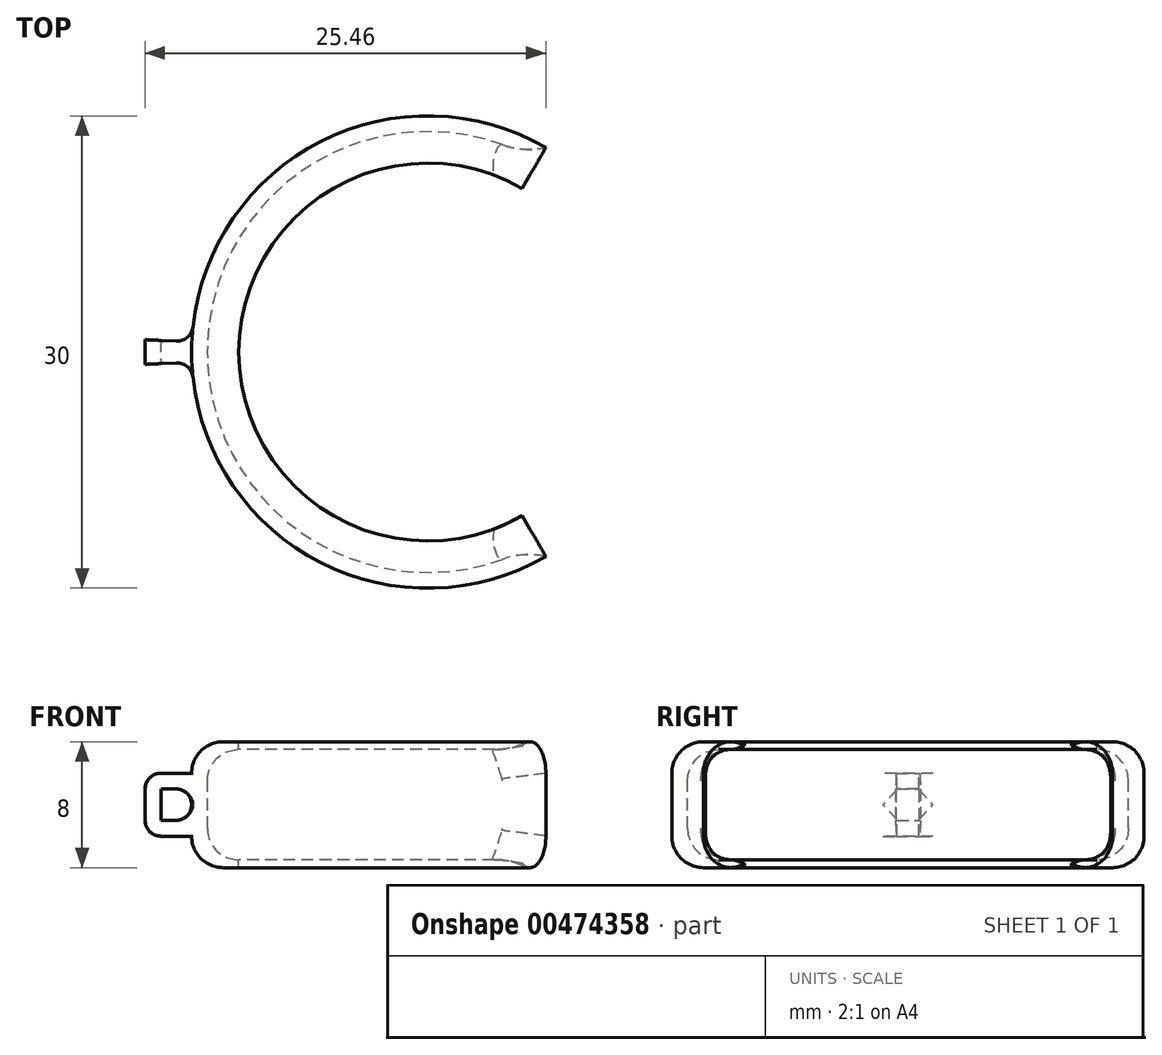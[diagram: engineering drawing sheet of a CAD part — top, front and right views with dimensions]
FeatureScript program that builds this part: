
annotation { "Feature Type Name" : "Feature", "Feature Type Description" : "" }
export const myFeature = defineFeature(function(context is Context, id is Id, definition is map)
    precondition{}
    {
        {
            var Q0;
            Q0=qCreatedBy(makeId("Front.planeOp"),FACE);
            var sketch = newSketch(context, id + "F0", { "sketchPlane" : qUnion([Q0])});
            skLineSegment(sketch, "E0", {"start": v(0, 12.3) * mm, "end": v(0, 0) * mm, "construction": true});
            skLineSegment(sketch, "E1", {"start": v(-12, -3.5) * mm, "end": v(-12, -3.5) * mm});
            skLineSegment(sketch, "E2", {"start": v(-14, 1.5) * mm, "end": v(-14, -1.5) * mm});
            skPoint(sketch, "E3.newPointB", {"position": v(-14, 3.5) * mm});
            skArc(sketch, "E3.filletArc", {"start": v(-12, 3.5) * mm, "mid": v(-13.41, 2.91) * mm, "end": v(-14, 1.5) * mm});
            skPoint(sketch, "E4.newPointA", {"position": v(-14, -3.5) * mm});
            skArc(sketch, "E4.filletArc", {"start": v(-14, -1.5) * mm, "mid": v(-13.41, -2.91) * mm, "end": v(-12, -3.5) * mm});
            skLineSegment(sketch, "E5", {"start": v(-12, 4) * mm, "end": v(-13, 4) * mm});
            skLineSegment(sketch, "E6", {"start": v(-15, 2) * mm, "end": v(-15, -2) * mm});
            skLineSegment(sketch, "E7", {"start": v(-13, -4) * mm, "end": v(-12, -4) * mm});
            skLineSegment(sketch, "E8", {"start": v(-12, -4) * mm, "end": v(-12, -3.5) * mm});
            skLineSegment(sketch, "E9", {"start": v(-12, 3.5) * mm, "end": v(-12, 4) * mm});
            skPoint(sketch, "E10.visualSharp", {"position": v(-15, 4) * mm});
            skArc(sketch, "E10.filletArc", {"start": v(-13, 4) * mm, "mid": v(-14.41, 3.41) * mm, "end": v(-15, 2) * mm});
            skPoint(sketch, "E11.visualSharp", {"position": v(-15, -4) * mm});
            skArc(sketch, "E11.filletArc", {"start": v(-15, -2) * mm, "mid": v(-14.41, -3.41) * mm, "end": v(-13, -4) * mm});
            skLineSegment(sketch, "E12", {"start": v(-15, 0) * mm, "end": v(0, 0) * mm, "construction": true});
            skSolve(sketch);
        }
        {
            var Q0;
            Q0 = qSketchRegion(id + "F0", true);
            var Q1;
            Q1=sQuery(id+"F0.wireOp",EDGE,"E0");
            revolve(context, id + "F1", {"entities" : qUnion([Q0]), "axis" : qUnion([Q1]), "revolveType" : RevolveType.SYMMETRIC, "angle" : 240 * degree});
        }
        {
            var Q0;
            Q0=qCreatedBy(makeId("Front.planeOp"),FACE);
            var sketch = newSketch(context, id + "F2", { "sketchPlane" : qUnion([Q0])});
            skLineSegment(sketch, "E13", {"start": v(0, 0) * mm, "end": v(-17.96, 0) * mm, "construction": true});
            skLineSegment(sketch, "E14", {"start": v(-14.96, -1) * mm, "end": v(-16.96, -1) * mm});
            skLineSegment(sketch, "E15", {"start": v(-16.96, -1) * mm, "end": v(-16.96, 1) * mm});
            skLineSegment(sketch, "E16", {"start": v(-16.96, 1) * mm, "end": v(-14.96, 1) * mm});
            skLineSegment(sketch, "E17", {"start": v(-14.96, 2) * mm, "end": v(-16.96, 2) * mm});
            skLineSegment(sketch, "E18", {"start": v(-17.96, 1) * mm, "end": v(-17.96, -1) * mm});
            skLineSegment(sketch, "E19", {"start": v(-16.96, -2) * mm, "end": v(-14.96, -2) * mm});
            skPoint(sketch, "E20.visualSharp", {"position": v(-17.96, 2) * mm});
            skArc(sketch, "E20.filletArc", {"start": v(-16.96, 2) * mm, "mid": v(-17.67, 1.7) * mm, "end": v(-17.96, 1) * mm});
            skPoint(sketch, "E21.visualSharp", {"position": v(-17.96, -2) * mm});
            skArc(sketch, "E21.filletArc", {"start": v(-17.96, -1) * mm, "mid": v(-17.67, -1.7) * mm, "end": v(-16.96, -2) * mm});
            skLineSegment(sketch, "E22", {"start": v(-14.96, 2) * mm, "end": v(-14.96, 1) * mm});
            skLineSegment(sketch, "E23", {"start": v(-14.96, -1) * mm, "end": v(-14.96, -2) * mm});
            skLineSegment(sketch, "E24", {"start": v(0, 0) * mm, "end": v(0, 2.12) * mm, "construction": true});
            skSolve(sketch);
        }
        {
            var Q0;
            Q0 = qSketchRegion(id + "F2", true);
            var Q1;
            Q1=sQuery(id+"F2.wireOp",EDGE,"E24");
            revolve(context, id + "F3", {"operationType" : NewBodyOperationType.ADD, "entities" : qUnion([Q0]), "axis" : qUnion([Q1]), "revolveType" : RevolveType.SYMMETRIC, "angle" : 5 * degree});
        }
        {
            var Q0;
            Q0=makeQuery(id+"F1.opRevolve","CAP_EDGE",EDGE,{"disambiguationData":[OSD([sQuery(id+"F0.wireOp",EDGE,"E2")])],"isStart":false});
            var Q1;
            Q1=makeQuery(id+"F1.opRevolve","CAP_EDGE",EDGE,{"disambiguationData":[OSD([sQuery(id+"F0.wireOp",EDGE,"E2")])],"isStart":true});
            var Q2;
            Q2=makeQuery(id+"F1.opRevolve","CAP_EDGE",EDGE,{"disambiguationData":[OSD([sQuery(id+"F0.wireOp",EDGE,"E3.filletArc")])],"isStart":true});
            var Q3;
            Q3=makeQuery(id+"F1.opRevolve","CAP_EDGE",EDGE,{"disambiguationData":[OSD([sQuery(id+"F0.wireOp",EDGE,"E4.filletArc")])],"isStart":true});
            var Q4;
            Q4=makeQuery(id+"F1.opRevolve","CAP_EDGE",EDGE,{"disambiguationData":[OSD([sQuery(id+"F0.wireOp",EDGE,"E4.filletArc")])],"isStart":false});
            var Q5;
            Q5=makeQuery(id+"F1.opRevolve","CAP_EDGE",EDGE,{"disambiguationData":[OSD([sQuery(id+"F0.wireOp",EDGE,"E3.filletArc")])],"isStart":false});
            fillet(context, id + "F4", {"entities" : qUnion([Q0, Q1, Q2, Q3, Q4, Q5]), "radius" : 5 * mm, "tangentPropagation" : true, "allowEdgeOverflow" : false});
        }
        {
            var Q0;
            Q0=makeQuery(id+"F3.boolean.opBoolean","INTERSECT",EDGE,{"disambiguationData":[OD(1.0)],"derivedFrom":[makeQuery(id+"F1.opRevolve","SWEPT_FACE",FACE,{"disambiguationData":[OSD([sQuery(id+"F0.wireOp",EDGE,"E6")])]}),makeQuery(id+"F3.opRevolve","CAP_FACE",FACE,{"disambiguationData":[OSD([sQuery(id+"F2.wireOp",EDGE,"E14"),sQuery(id+"F2.wireOp",EDGE,"E15"),sQuery(id+"F2.wireOp",EDGE,"E16"),sQuery(id+"F2.wireOp",EDGE,"E17"),sQuery(id+"F2.wireOp",EDGE,"E18"),sQuery(id+"F2.wireOp",EDGE,"E19"),sQuery(id+"F2.wireOp",EDGE,"E20.filletArc"),sQuery(id+"F2.wireOp",EDGE,"E21.filletArc"),sQuery(id+"F2.wireOp",EDGE,"E22"),sQuery(id+"F2.wireOp",EDGE,"E23")])],"isStart":false})]});
            var Q1;
            Q1=makeQuery(id+"F3.boolean.opBoolean","INTERSECT",EDGE,{"disambiguationData":[OD(0.0)],"derivedFrom":[makeQuery(id+"F1.opRevolve","SWEPT_FACE",FACE,{"disambiguationData":[OSD([sQuery(id+"F0.wireOp",EDGE,"E6")])]}),makeQuery(id+"F3.opRevolve","CAP_FACE",FACE,{"disambiguationData":[OSD([sQuery(id+"F2.wireOp",EDGE,"E14"),sQuery(id+"F2.wireOp",EDGE,"E15"),sQuery(id+"F2.wireOp",EDGE,"E16"),sQuery(id+"F2.wireOp",EDGE,"E17"),sQuery(id+"F2.wireOp",EDGE,"E18"),sQuery(id+"F2.wireOp",EDGE,"E19"),sQuery(id+"F2.wireOp",EDGE,"E20.filletArc"),sQuery(id+"F2.wireOp",EDGE,"E21.filletArc"),sQuery(id+"F2.wireOp",EDGE,"E22"),sQuery(id+"F2.wireOp",EDGE,"E23")])],"isStart":false})]});
            var Q2;
            {var subQ0=sQuery(id+"F0.wireOp",EDGE,"E10.filletArc");Q2=makeQuery(id+"F3.boolean.opBoolean","SPLIT",EDGE,{"disambiguationData":[topologyDisambiguationEdgeConnected([makeQuery(id+"F1.opRevolve","SWEPT_FACE",FACE,{"disambiguationData":[OSD([subQ0])]}),makeQuery(id+"F3.opRevolve","SWEPT_FACE",FACE,{"disambiguationData":[OSD([sQuery(id+"F2.wireOp",EDGE,"E17")])]})])],"derivedFrom":makeQuery(id+"F1.opRevolve","SWEPT_EDGE",EDGE,{"disambiguationData":[OSD([sQuery(id+"F0.wireOp",EDGE,"E6"),subQ0])]})});}
            var Q3;
            Q3=makeQuery(id+"F3.boolean.opBoolean","INTERSECT",EDGE,{"disambiguationData":[OD(1.0)],"derivedFrom":[makeQuery(id+"F1.opRevolve","SWEPT_FACE",FACE,{"disambiguationData":[OSD([sQuery(id+"F0.wireOp",EDGE,"E6")])]}),makeQuery(id+"F3.opRevolve","CAP_FACE",FACE,{"disambiguationData":[OSD([sQuery(id+"F2.wireOp",EDGE,"E14"),sQuery(id+"F2.wireOp",EDGE,"E15"),sQuery(id+"F2.wireOp",EDGE,"E16"),sQuery(id+"F2.wireOp",EDGE,"E17"),sQuery(id+"F2.wireOp",EDGE,"E18"),sQuery(id+"F2.wireOp",EDGE,"E19"),sQuery(id+"F2.wireOp",EDGE,"E20.filletArc"),sQuery(id+"F2.wireOp",EDGE,"E21.filletArc"),sQuery(id+"F2.wireOp",EDGE,"E22"),sQuery(id+"F2.wireOp",EDGE,"E23")])],"isStart":true})]});
            var Q4;
            Q4=makeQuery(id+"F3.boolean.opBoolean","INTERSECT",EDGE,{"disambiguationData":[OD(0.0)],"derivedFrom":[makeQuery(id+"F1.opRevolve","SWEPT_FACE",FACE,{"disambiguationData":[OSD([sQuery(id+"F0.wireOp",EDGE,"E6")])]}),makeQuery(id+"F3.opRevolve","CAP_FACE",FACE,{"disambiguationData":[OSD([sQuery(id+"F2.wireOp",EDGE,"E14"),sQuery(id+"F2.wireOp",EDGE,"E15"),sQuery(id+"F2.wireOp",EDGE,"E16"),sQuery(id+"F2.wireOp",EDGE,"E17"),sQuery(id+"F2.wireOp",EDGE,"E18"),sQuery(id+"F2.wireOp",EDGE,"E19"),sQuery(id+"F2.wireOp",EDGE,"E20.filletArc"),sQuery(id+"F2.wireOp",EDGE,"E21.filletArc"),sQuery(id+"F2.wireOp",EDGE,"E22"),sQuery(id+"F2.wireOp",EDGE,"E23")])],"isStart":true})]});
            var Q5;
            {var subQ0=sQuery(id+"F0.wireOp",EDGE,"E11.filletArc");Q5=makeQuery(id+"F3.boolean.opBoolean","SPLIT",EDGE,{"disambiguationData":[topologyDisambiguationEdgeConnected([makeQuery(id+"F1.opRevolve","SWEPT_FACE",FACE,{"disambiguationData":[OSD([subQ0])]}),makeQuery(id+"F3.opRevolve","SWEPT_FACE",FACE,{"disambiguationData":[OSD([sQuery(id+"F2.wireOp",EDGE,"E19")])]})])],"derivedFrom":makeQuery(id+"F1.opRevolve","SWEPT_EDGE",EDGE,{"disambiguationData":[OSD([sQuery(id+"F0.wireOp",EDGE,"E6"),subQ0])]})});}
            var Q6;
            Q6=makeQuery(id+"F3.boolean.opBoolean","INTERSECT",EDGE,{"derivedFrom":[makeQuery(id+"F1.opRevolve","SWEPT_FACE",FACE,{"disambiguationData":[OSD([sQuery(id+"F0.wireOp",EDGE,"E6")])]}),makeQuery(id+"F3.opRevolve","SWEPT_FACE",FACE,{"disambiguationData":[OSD([sQuery(id+"F2.wireOp",EDGE,"E14")])]})]});
            var Q7;
            Q7=makeQuery(id+"F3.boolean.opBoolean","INTERSECT",EDGE,{"derivedFrom":[makeQuery(id+"F1.opRevolve","SWEPT_FACE",FACE,{"disambiguationData":[OSD([sQuery(id+"F0.wireOp",EDGE,"E6")])]}),makeQuery(id+"F3.opRevolve","SWEPT_FACE",FACE,{"disambiguationData":[OSD([sQuery(id+"F2.wireOp",EDGE,"E16")])]})]});
            fillet(context, id + "F5", {"entities" : qUnion([Q0, Q1, Q2, Q3, Q4, Q5, Q6, Q7]), "radius" : 1 * mm, "tangentPropagation" : true, "allowEdgeOverflow" : false});
        }
    });
